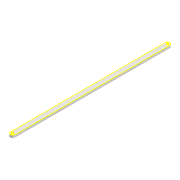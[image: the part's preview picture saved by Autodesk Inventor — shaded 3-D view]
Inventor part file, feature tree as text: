
AUTODESK INVENTOR PART (.ipt)
format: ipt  version: 2022 (Build 260153000, 153)  size: 91,648 bytes
history: native  units: mm
features: sketch x2, extrude x1, projected_geometry x1
ambient origin geometry x8: Origin, YZ Plane, XZ Plane, XY Plane, X Axis, Y Axis, Z Axis, Center Point
bodies: Solid1 (feature_tree)
feature tree (4):
  extrude  "Extrusion1"  Depth=8.0mm
  sketch  "Sketch2"  dims[d2=3.0mm d3=3.0mm d4=4.5mm d5=0.0mm]
  sketch  "Sketch1"  dims[d0=263.803mm d1=8.0mm]
  projected_geometry  "Projected Loop1"
